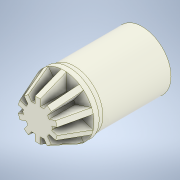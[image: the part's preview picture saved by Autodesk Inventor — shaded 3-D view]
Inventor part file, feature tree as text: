
AUTODESK INVENTOR PART (.ipt)
format: ipt  version: 2022.6 (Build 266554000, 554)  size: 264,192 bytes
history: native  units: mm
features: extrude x6, thicken_offset x2, chamfer x1, hole x1, pattern_circular x1, fillet x1
ambient origin geometry x8: Origin, YZ Plane, XZ Plane, XY Plane, X Axis, Y Axis, Z Axis, Center Point
bodies: Solid1 (feature_tree)
feature tree (12):
  extrude  "Adapter"  Depth=11.0mm
  extrude  "Motor Shaft Profile"  Depth=1.0mm TaperAngle=0.0deg
  chamfer  "Chamfer1"  Distance=13.0mm
  thicken_offset  "Thicken5"
  thicken_offset  "Thicken6"
  hole  "Hole6"  [1 undecoded]
  extrude  "Extrusion5"  Depth=12.0mm TaperAngle=0.0deg
  extrude  "Extrusion6"  Depth=0.2mm
  extrude  "Extrusion7"  Depth=2.0mm TaperAngle=45.0deg
  pattern_circular  "Circular Pattern1"  [2 undecoded]
  extrude  "Extrusion8"  Depth=0.2mm
  fillet  "Fillet1"  Radius=11.5mm
note: 3 required parameter values undecoded (feature->parameter linkage not recoverable at this tier; creation-order binding heuristic only, values carry confidence <= 0.55)
